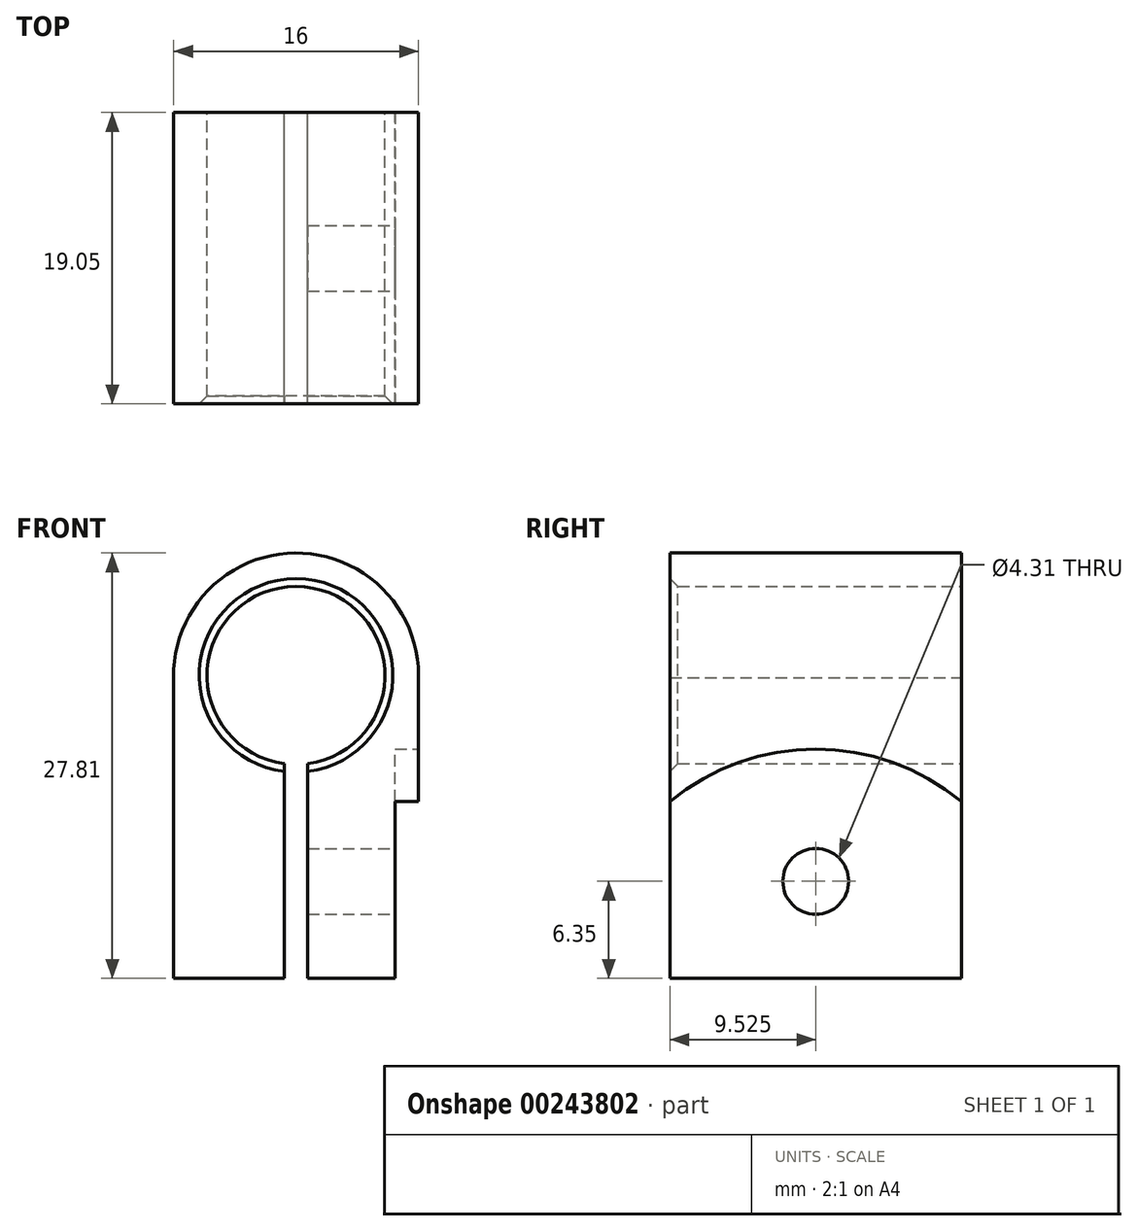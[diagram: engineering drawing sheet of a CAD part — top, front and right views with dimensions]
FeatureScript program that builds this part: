
annotation { "Feature Type Name" : "Feature", "Feature Type Description" : "" }
export const myFeature = defineFeature(function(context is Context, id is Id, definition is map)
    precondition{}
    {
        {
            var Q0;
            Q0=qCreatedBy(makeId("Front.planeOp"),FACE);
            var sketch = newSketch(context, id + "F0", { "sketchPlane" : qUnion([Q0])});
            skArc(sketch, "E0", {"start": v(8, 19.81) * mm, "mid": v(-0.07, 27.81) * mm, "end": v(-8, 19.67) * mm});
            skLineSegment(sketch, "E1", {"start": v(0.76, 0) * mm, "end": v(8, 0) * mm});
            skLineSegment(sketch, "E2", {"start": v(8, 19.81) * mm, "end": v(8, 0) * mm});
            skLineSegment(sketch, "E3", {"start": v(-8, 19.67) * mm, "end": v(-8, 0) * mm});
            skLineSegment(sketch, "E4", {"start": v(-8, 0) * mm, "end": v(-0.76, 0) * mm});
            skArc(sketch, "E5", {"start": v(0.76, 14.05) * mm, "mid": v(0, 25.63) * mm, "end": v(-0.76, 14.05) * mm});
            skLineSegment(sketch, "E6.0", {"start": v(-0.76, 14.05) * mm, "end": v(-0.76, 0) * mm});
            skLineSegment(sketch, "E7.0", {"start": v(0.76, 14.05) * mm, "end": v(0.76, 0) * mm});
            skSolve(sketch);
        }
        {
            var Q0;
            Q0=makeQuery(id+"F0.imprint","IMPRINT",FACE,{"disambiguationData":[TD([[makeQuery(id+"F0.imprint","IMPRINT",EDGE,{"derivedFrom":sQuery(id+"F0.wireOp",EDGE,"E0")}),1.0]])]});
            extrude(context, id + "F1", {"entities" : qUnion([Q0]), "depth" : 19.05 * mm});
        }
        {
            var Q0;
            Q0=makeQuery(id+"F1.opExtrude","CAP_EDGE",EDGE,{"disambiguationData":[OSD([sQuery(id+"F0.wireOp",EDGE,"E5")])],"isStart":false});
            chamfer(context, id + "F2", {"entities" : qUnion([Q0]), "width" : 0.5 * mm, "tangentPropagation" : true});
        }
        {
            var Q0;
            Q0=makeQuery(id+"F1.opExtrude","SWEPT_FACE",FACE,{"disambiguationData":[OSD([sQuery(id+"F0.wireOp",EDGE,"E2")])]});
            var sketch = newSketch(context, id + "F3", { "sketchPlane" : qUnion([Q0])});
            skArc(sketch, "E8", {"start": v(0, 11.57) * mm, "mid": v(-9.52, 14.99) * mm, "end": v(-19.05, 11.57) * mm});
            skLineSegment(sketch, "E9", {"start": v(-19.05, 0) * mm, "end": v(-19.05, 11.57) * mm});
            skLineSegment(sketch, "E10", {"start": v(0, 0) * mm, "end": v(0, 11.57) * mm});
            skLineSegment(sketch, "E11", {"start": v(-19.05, 0) * mm, "end": v(0, 0) * mm});
            skSolve(sketch);
        }
        {
            var Q0;
            Q0=makeQuery(id+"F3.imprint","IMPRINT",FACE,{"disambiguationData":[TD([[makeQuery(id+"F3.imprint","IMPRINT",EDGE,{"derivedFrom":sQuery(id+"F3.wireOp",EDGE,"E8")}),1.0]])]});
            extrude(context, id + "F4", {"entities" : qUnion([Q0]), "operationType" : NewBodyOperationType.REMOVE, "oppositeDirection" : true, "depth" : 1.52 * mm});
        }
        {
            var Q0;
            Q0=makeQuery(id+"F4.boolean.opBoolean","COPY",FACE,{"derivedFrom":makeQuery(id+"F4.opExtrude","CAP_FACE",FACE,{"disambiguationData":[OSD([sQuery(id+"F3.wireOp",EDGE,"E8"),sQuery(id+"F3.wireOp",EDGE,"E9"),sQuery(id+"F3.wireOp",EDGE,"E10"),sQuery(id+"F3.wireOp",EDGE,"E11")])],"isStart":false})});
            var sketch = newSketch(context, id + "F5", { "sketchPlane" : qUnion([Q0])});
            skPoint(sketch, "E12", {"position": v(-9.53, 6.35) * mm});
            skSolve(sketch);
        }
        {
            var Q0;
            Q0=sQuery(id+"F5.wireOp",VERTEX,"E12");
            var Q1;
            Q1=makeQuery(id+"F1.opExtrude","SWEPT_BODY",BODY,{"disambiguationData":[OSD([sQuery(id+"F0.wireOp",EDGE,"E0"),sQuery(id+"F0.wireOp",EDGE,"E1"),sQuery(id+"F0.wireOp",EDGE,"E2"),sQuery(id+"F0.wireOp",EDGE,"E3"),sQuery(id+"F0.wireOp",EDGE,"E4"),sQuery(id+"F0.wireOp",EDGE,"E5"),sQuery(id+"F0.wireOp",EDGE,"E6.0"),sQuery(id+"F0.wireOp",EDGE,"E7.0")])]});
            hole(context, id + "F6", {"style" : HoleStyle.SIMPLE, "endStyle" : HoleEndStyle.BLIND, "standardTappedOrClearance" : lookupTablePath({ "standard" : "ANSI", "engagement" : "50%", "pitch" : "32 tpi", "size" : "#10", "type" : "Tapped" }), "standardBlindInLast" : lookupTablePath({ "standard" : "ANSI", "engagement" : "50%", "pitch" : "32 tpi", "size" : "#10", "type" : "Tapped" }), "holeDiameter" : 4.3 * mm, "holeDepth" : 5.84 * mm, "locations" : qUnion([Q0]), "scope" : qUnion([Q1]), "majorDiameter" : 4.83 * mm});
        }
    });
